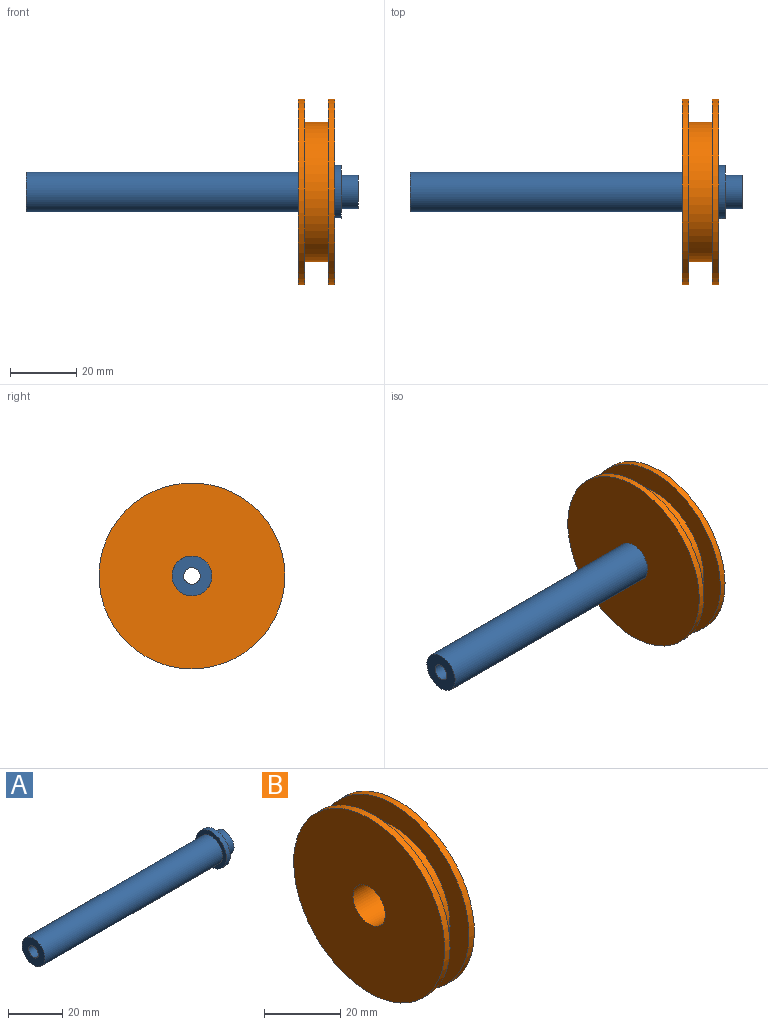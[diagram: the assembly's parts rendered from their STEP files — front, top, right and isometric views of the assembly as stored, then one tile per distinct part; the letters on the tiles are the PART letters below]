
ASSEMBLY  parts=2 mates=1
PART A: 8 faces, bbox 100x16x16 mm
  f0: cylinder r=2.5mm len=100mm, axis (-1,0,0), area 1570.8mm2, adj f1,f7
  f1: plane 10x10mm, normal (1,0,0), area 58.9mm2, adj f0,f2
  f2: cylinder r=5mm len=10mm, axis (-1,0,0), area 157.1mm2, adj f1,f3
  f3: plane 16x16mm, normal (1,0,0), area 122.5mm2, adj f2,f4
  f4: cylinder r=8mm len=16mm, axis (-1,0,0), area 100.5mm2, adj f3,f5
  f5: plane 16x16mm, normal (-1,0,0), area 88mm2, adj f4,f6
  f6: cylinder r=6mm len=93mm, axis (-1,0,0), area 3506mm2, adj f5,f7
  f7: plane 12x12mm, normal (-1,0,0), area 93.5mm2, adj f0,f6
PART B: 8 faces, bbox 11x56x56 mm
  f0: cylinder r=6mm len=12mm, axis (-1,0,0), area 414.7mm2, adj f1,f7
  f1: plane 56x56mm, normal (1,0,0), area 2349.9mm2, adj f0,f2
  f2: cylinder r=28mm len=56mm, axis (-1,0,0), area 351.9mm2, adj f1,f3
  f3: plane 56x56mm, normal (-1,0,0), area 1077.6mm2, adj f2,f4
  f4: cylinder r=21mm len=42mm, axis (-1,0,0), area 923.6mm2, adj f3,f5
  f5: plane 56x56mm, normal (1,0,0), area 1077.6mm2, adj f4,f6
  f6: cylinder r=28mm len=56mm, axis (-1,0,0), area 351.9mm2, adj f5,f7
  f7: plane 56x56mm, normal (-1,0,0), area 2349.9mm2, adj f0,f6
PLACE A t=(0.36,-10.53,23.87)mm fixed
PLACE B rot(axis=(0,-0.95,0.3),180deg) t=(48.5,-8.09,53.16)mm
MATE cylindrical A.f0 <-> B.f0  axis (-1,0,0) through (-35.5,-10.53,49.64)mm
